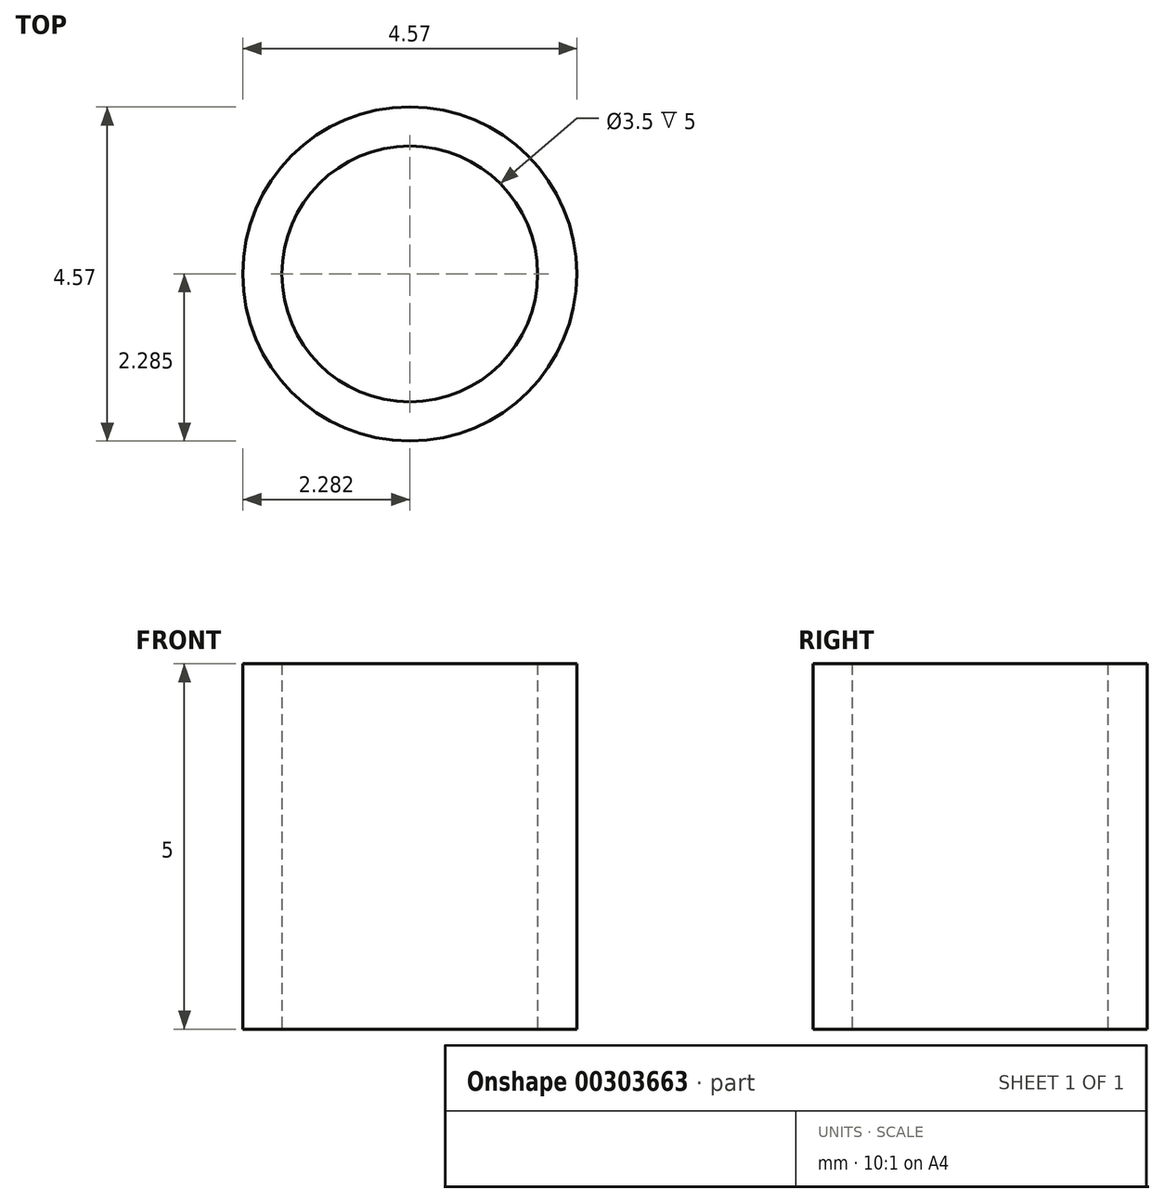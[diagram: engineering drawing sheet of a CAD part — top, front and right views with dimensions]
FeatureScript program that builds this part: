
annotation { "Feature Type Name" : "Feature", "Feature Type Description" : "" }
export const myFeature = defineFeature(function(context is Context, id is Id, definition is map)
    precondition{}
    {
        {
            var Q0;
            Q0=qCreatedBy(makeId("Top.planeOp"),FACE);
            var sketch = newSketch(context, id + "F0", { "sketchPlane" : qUnion([Q0])});
            skLineSegment(sketch, "E0", {"start": v(5.75, 0) * mm, "end": v(-0.25, 0) * mm});
            skCircle(sketch, "E1", {"center": v(3.09, 0) * mm, "radius": 1.8 * mm, "construction": true});
            skCircle(sketch, "E2", {"center": v(3.09, 0) * mm, "radius": 1.4 * mm});
            skPoint(sketch, "E3", {"position": v(1.29, 0) * mm});
            skPoint(sketch, "E4", {"position": v(0.4, 0) * mm});
            skPoint(sketch, "E5", {"position": v(1.69, 0) * mm});
            skLineSegment(sketch, "E6", {"start": v(3.09, 0) * mm, "end": v(-0.25, 0) * mm});
            skPoint(sketch, "E7", {"position": v(4.49, 0) * mm});
            skCircle(sketch, "E8", {"center": v(3.09, 0) * mm, "radius": 2.29 * mm});
            skLineSegment(sketch, "E9", {"start": v(10.54, -3.53) * mm, "end": v(4.2, -3.53) * mm});
            skCircle(sketch, "E10", {"center": v(7.88, -3.53) * mm, "radius": 1.8 * mm, "construction": true});
            skCircle(sketch, "E11", {"center": v(7.88, -3.53) * mm, "radius": 1.75 * mm});
            skPoint(sketch, "E12", {"position": v(6.08, -3.53) * mm});
            skPoint(sketch, "E13", {"position": v(5.2, -3.53) * mm});
            skPoint(sketch, "E14", {"position": v(6.13, -3.53) * mm});
            skLineSegment(sketch, "E15", {"start": v(7.88, -3.53) * mm, "end": v(4.54, -3.53) * mm});
            skPoint(sketch, "E16", {"position": v(9.63, -3.53) * mm});
            skCircle(sketch, "E17", {"center": v(7.88, -3.53) * mm, "radius": 2.29 * mm});
            skSolve(sketch);
        }
        {
            var Q0;
            {var subQ0=sQuery(id+"F0.wireOp",EDGE,"E17");var subQ1=sQuery(id+"F0.wireOp",EDGE,"E9");var subQ2=makeQuery(id+"F0.imprint","INTERSECT",VERTEX,{"derivedFrom":[subQ1,subQ0]});Q0=makeQuery(id+"F0.imprint","IMPRINT",FACE,{"disambiguationData":[TD([[makeQuery(id+"F0.imprint","IMPRINT",EDGE,{"disambiguationData":[TD([[subQ2,-1.0]])],"derivedFrom":subQ1}),-1.0]])]});}
            var Q1;
            {var subQ0=sQuery(id+"F0.wireOp",EDGE,"E17");var subQ1=sQuery(id+"F0.wireOp",EDGE,"E9");var subQ2=makeQuery(id+"F0.imprint","INTERSECT",VERTEX,{"derivedFrom":[subQ1,subQ0]});Q1=makeQuery(id+"F0.imprint","IMPRINT",FACE,{"disambiguationData":[TD([[makeQuery(id+"F0.imprint","IMPRINT",EDGE,{"disambiguationData":[TD([[subQ2,-1.0]])],"derivedFrom":subQ1}),1.0]])]});}
            extrude(context, id + "F1", {"entities" : qUnion([Q0, Q1]), "depth" : 5 * mm});
        }
    });
